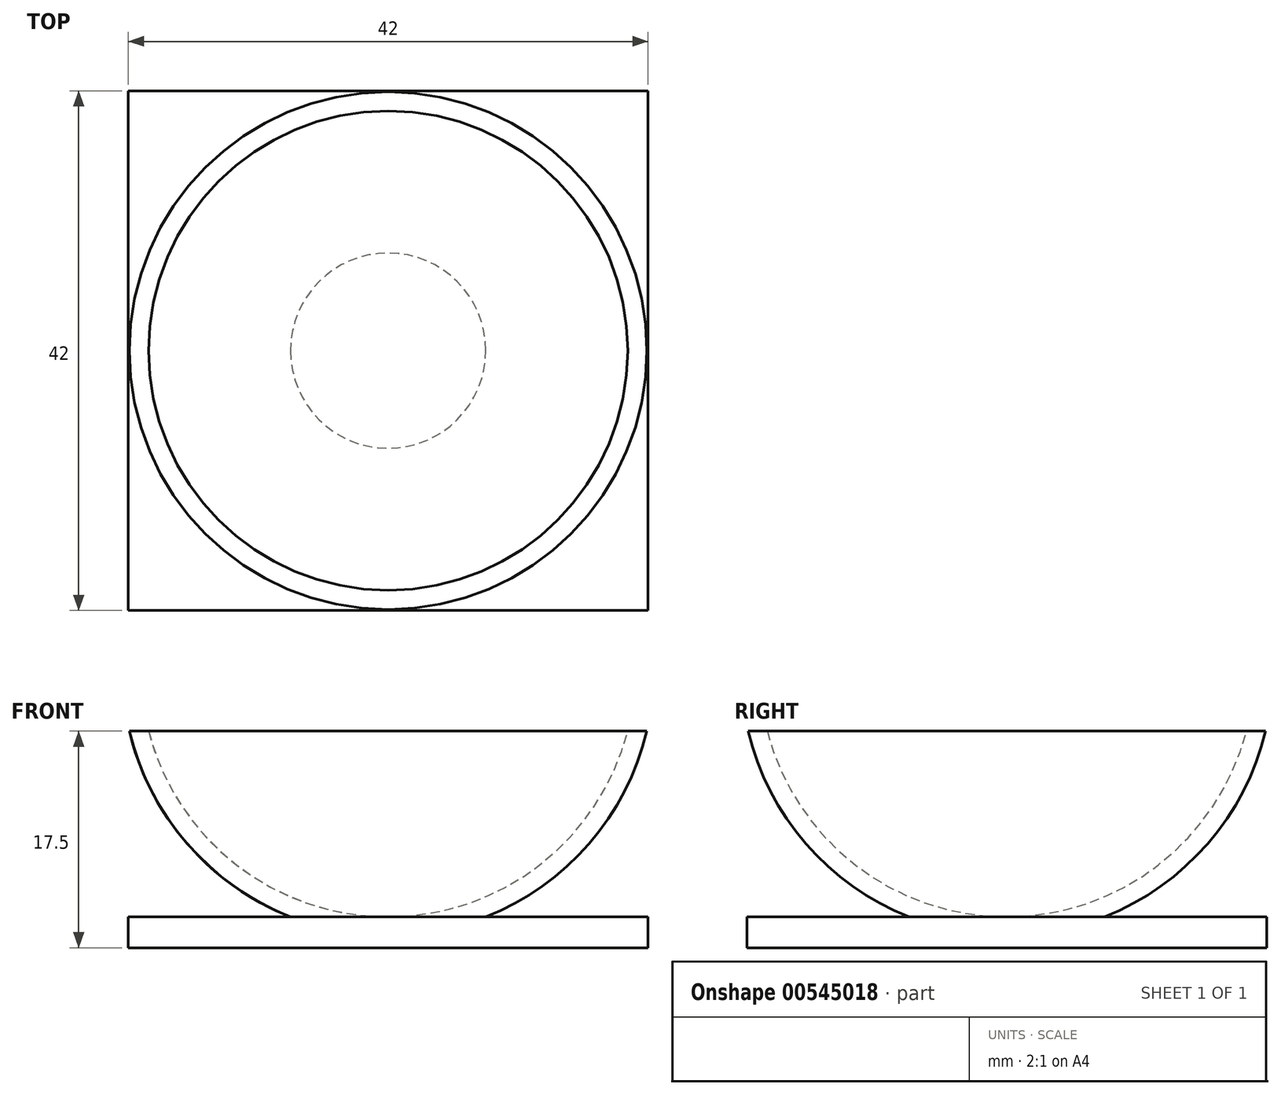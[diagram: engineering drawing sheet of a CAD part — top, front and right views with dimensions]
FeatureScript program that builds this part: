
annotation { "Feature Type Name" : "Feature", "Feature Type Description" : "" }
export const myFeature = defineFeature(function(context is Context, id is Id, definition is map)
    precondition{}
    {
        {
            var Q0;
            Q0=qCreatedBy(makeId("Top.planeOp"),FACE);
            var sketch = newSketch(context, id + "F0", { "sketchPlane" : qUnion([Q0])});
            skLineSegment(sketch, "E0.bottom", {"start": v(-21, 21) * mm, "end": v(21, 21) * mm});
            skLineSegment(sketch, "E0.top", {"start": v(-21, -21) * mm, "end": v(21, -21) * mm});
            skLineSegment(sketch, "E0.left", {"start": v(-21, 21) * mm, "end": v(-21, -21) * mm});
            skLineSegment(sketch, "E0.right", {"start": v(21, 21) * mm, "end": v(21, -21) * mm});
            skPoint(sketch, "E1", {"position": v(0, 21) * mm});
            skPoint(sketch, "E2", {"position": v(0, -21) * mm});
            skPoint(sketch, "E3", {"position": v(-21, 0) * mm});
            skPoint(sketch, "E4", {"position": v(21, 0) * mm});
            skLineSegment(sketch, "E5", {"start": v(0, 21) * mm, "end": v(0, -21) * mm, "construction": true});
            skLineSegment(sketch, "E6", {"start": v(-21, 0) * mm, "end": v(21, 0) * mm, "construction": true});
            skPoint(sketch, "E7", {"position": v(0, 0) * mm});
            skSolve(sketch);
        }
        {
            var Q0;
            Q0 = qSketchRegion(id + "F0", true);
            extrude(context, id + "F1", {"entities" : qUnion([Q0]), "depth" : 2.5 * mm, "offsetDistance" : 25 * mm});
        }
        {
            var Q0;
            Q0=qCreatedBy(makeId("Front.planeOp"),FACE);
            var sketch = newSketch(context, id + "F2", { "sketchPlane" : qUnion([Q0])});
            skLineSegment(sketch, "E8", {"start": v(0, 0) * mm, "end": v(0, 17.5) * mm});
            skArc(sketch, "E9", {"start": v(-19.36, 17.5) * mm, "mid": v(0, 2.5) * mm, "end": v(19.36, 17.5) * mm});
            skArc(sketch, "E10", {"start": v(-20.91, 17.5) * mm, "mid": v(0, 1) * mm, "end": v(20.91, 17.5) * mm});
            skPoint(sketch, "E11", {"position": v(0, 17.5) * mm});
            skPoint(sketch, "E12", {"position": v(-19.36, 17.5) * mm});
            skPoint(sketch, "E13", {"position": v(-20.91, 17.5) * mm});
            skPoint(sketch, "E14", {"position": v(19.36, 17.5) * mm});
            skPoint(sketch, "E15", {"position": v(20.91, 17.5) * mm});
            skPoint(sketch, "E16.orphan", {"position": v(-21.5, 22.5) * mm});
            skPoint(sketch, "E17.orphan", {"position": v(-20, 22.5) * mm});
            skPoint(sketch, "E18.orphan", {"position": v(20, 22.5) * mm});
            skPoint(sketch, "E19.orphan", {"position": v(21.5, 22.5) * mm});
            skLineSegment(sketch, "E20", {"start": v(-20.91, 17.5) * mm, "end": v(-19.36, 17.5) * mm});
            skLineSegment(sketch, "E21", {"start": v(19.36, 17.5) * mm, "end": v(20.91, 17.5) * mm});
            skSolve(sketch);
        }
        {
            var Q0;
            {var subQ5=sQuery(id+"F2.wireOp",EDGE,"E20");Q0=makeQuery(id+"F2.imprint","IMPRINT",FACE,{"disambiguationData":[TD([[makeQuery(id+"F2.imprint","IMPRINT",EDGE,{"derivedFrom":subQ5}),-1.0]])]});}
            var Q1;
            Q1=sQuery(id+"F2.wireOp",EDGE,"E8");
            revolve(context, id + "F3", {"operationType" : NewBodyOperationType.ADD, "entities" : qUnion([Q0]), "axis" : qUnion([Q1]), "revolveType" : RevolveType.FULL});
        }
    });
